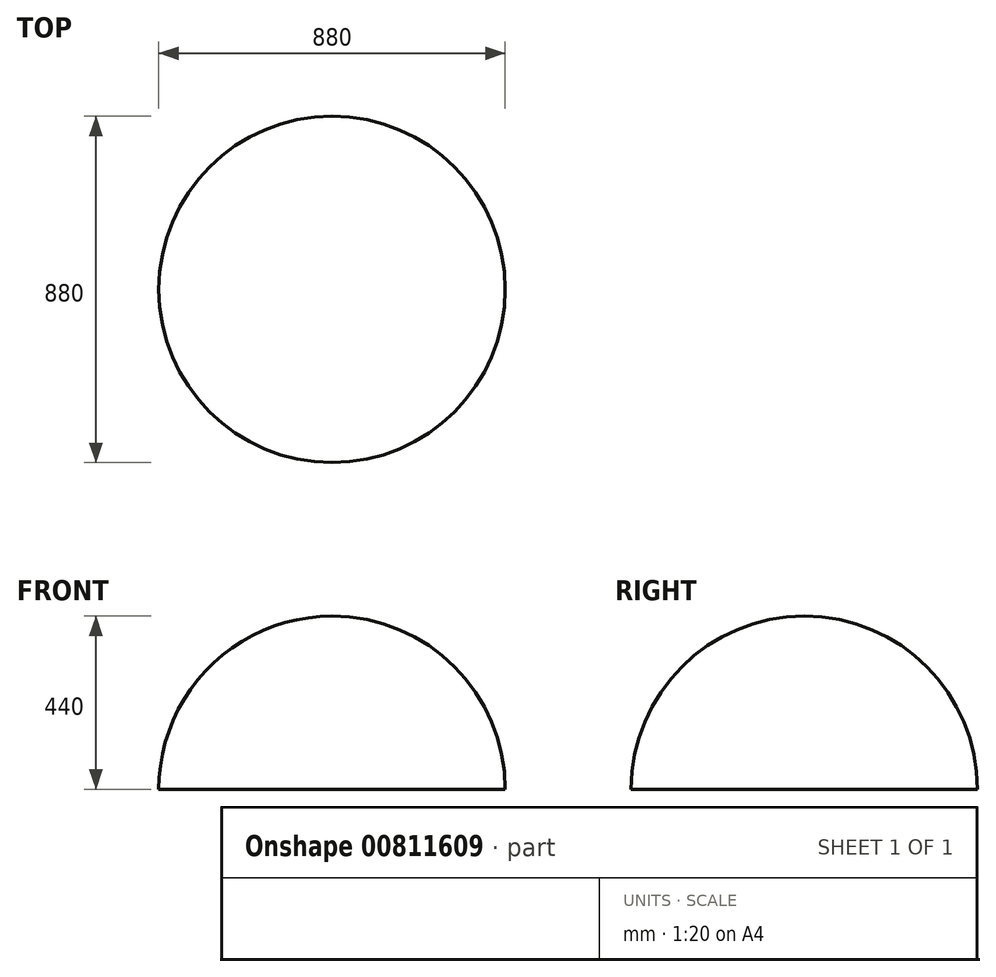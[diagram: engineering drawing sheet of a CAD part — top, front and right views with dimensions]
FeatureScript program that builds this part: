
annotation { "Feature Type Name" : "Feature", "Feature Type Description" : "" }
export const myFeature = defineFeature(function(context is Context, id is Id, definition is map)
    precondition{}
    {
        {
            var Q0;
            Q0=qCreatedBy(makeId("Front.planeOp"),FACE);
            var sketch = newSketch(context, id + "F0", { "sketchPlane" : qUnion([Q0])});
            skArc(sketch, "E0", {"start": v(0, 440) * mm, "mid": v(-311.13, 311.13) * mm, "end": v(-440, 0) * mm});
            skLineSegment(sketch, "E1", {"start": v(-440, 0) * mm, "end": v(0, 0) * mm});
            skPoint(sketch, "E2.orphan", {"position": v(-574.57, 0) * mm});
            skLineSegment(sketch, "E3", {"start": v(0, 440) * mm, "end": v(0, 0) * mm});
            skSolve(sketch);
        }
        {
            var Q0;
            Q0=makeQuery(id+"F0.imprint","IMPRINT",FACE,{"disambiguationData":[TD([[makeQuery(id+"F0.imprint","IMPRINT",EDGE,{"derivedFrom":sQuery(id+"F0.wireOp",EDGE,"E0")}),1.0]])]});
            var Q1;
            Q1=sQuery(id+"F0.wireOp",EDGE,"E3");
            revolve(context, id + "F1", {"surfaceOperationType" : NewSurfaceOperationType.NEW, "entities" : qUnion([Q0]), "axis" : qUnion([Q1]), "revolveType" : RevolveType.FULL});
        }
    });
